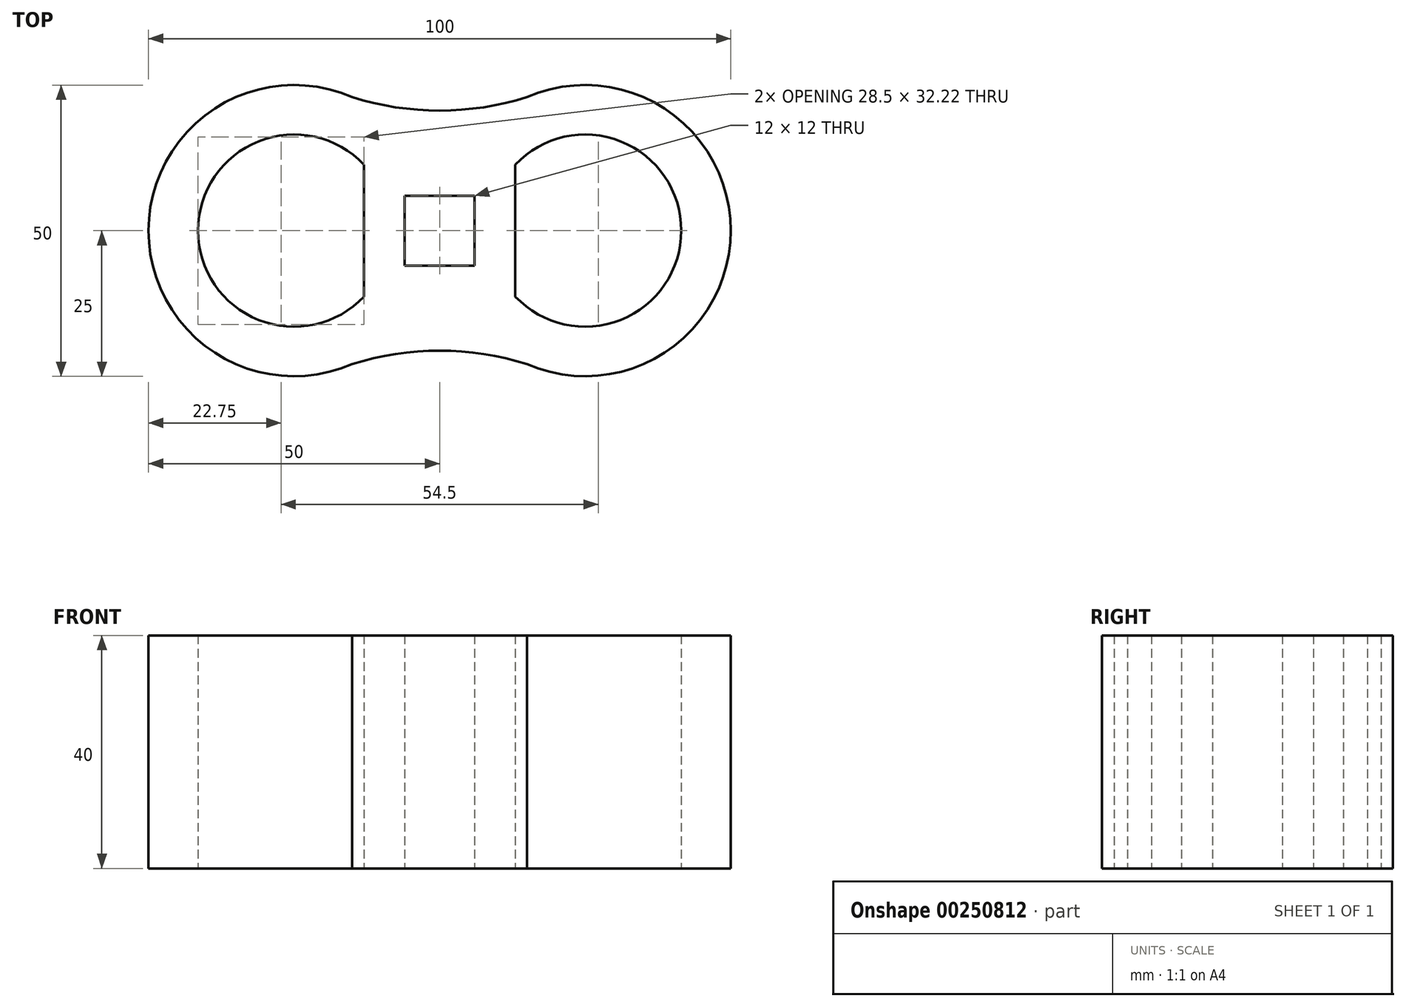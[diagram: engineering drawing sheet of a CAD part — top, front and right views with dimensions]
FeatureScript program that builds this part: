
annotation { "Feature Type Name" : "Feature", "Feature Type Description" : "" }
export const myFeature = defineFeature(function(context is Context, id is Id, definition is map)
    precondition{}
    {
        {
            var Q0;
            Q0=qCreatedBy(makeId("Top.planeOp"),FACE);
            var sketch = newSketch(context, id + "F0", { "sketchPlane" : qUnion([Q0])});
            skLineSegment(sketch, "E0.bottom", {"start": v(6, -6) * mm, "end": v(-6, -6) * mm});
            skLineSegment(sketch, "E0.top", {"start": v(6, 6) * mm, "end": v(-6, 6) * mm});
            skLineSegment(sketch, "E0.left", {"start": v(6, -6) * mm, "end": v(6, 6) * mm});
            skLineSegment(sketch, "E0.right", {"start": v(-6, -6) * mm, "end": v(-6, 6) * mm});
            skPoint(sketch, "E0.middle", {"position": v(0, 0) * mm});
            skArc(sketch, "E1", {"start": v(-15.02, 22.92) * mm, "mid": v(-50, 0) * mm, "end": v(-15.02, -22.92) * mm});
            skArc(sketch, "E2", {"start": v(-13, 11.32) * mm, "mid": v(-41.5, 0) * mm, "end": v(-13, -11.32) * mm});
            skArc(sketch, "E3.MirrorC", {"start": v(13, 11.32) * mm, "mid": v(41.5, 0) * mm, "end": v(13, -11.32) * mm});
            skArc(sketch, "E4.MirrorC", {"start": v(15.02, 22.92) * mm, "mid": v(50, 0) * mm, "end": v(15.02, -22.92) * mm});
            skArc(sketch, "E5", {"start": v(-18.34, 24.1) * mm, "mid": v(0, 20.61) * mm, "end": v(18.34, 24.1) * mm});
            skArc(sketch, "E6.MirrorCS", {"start": v(-18.34, -24.1) * mm, "mid": v(0, -20.61) * mm, "end": v(18.34, -24.1) * mm});
            skLineSegment(sketch, "E7", {"start": v(-13, -11.32) * mm, "end": v(-13, 11.32) * mm});
            skLineSegment(sketch, "E8.MirrorCS", {"start": v(13, -11.32) * mm, "end": v(13, 11.32) * mm});
            skPoint(sketch, "E9.orphan", {"position": v(-13, 0) * mm});
            skSolve(sketch);
        }
        {
            var Q0;
            Q0 = qSketchRegion(id + "F0", true);
            extrude(context, id + "F1", {"entities" : qUnion([Q0]), "depth" : 40 * mm});
        }
    });
